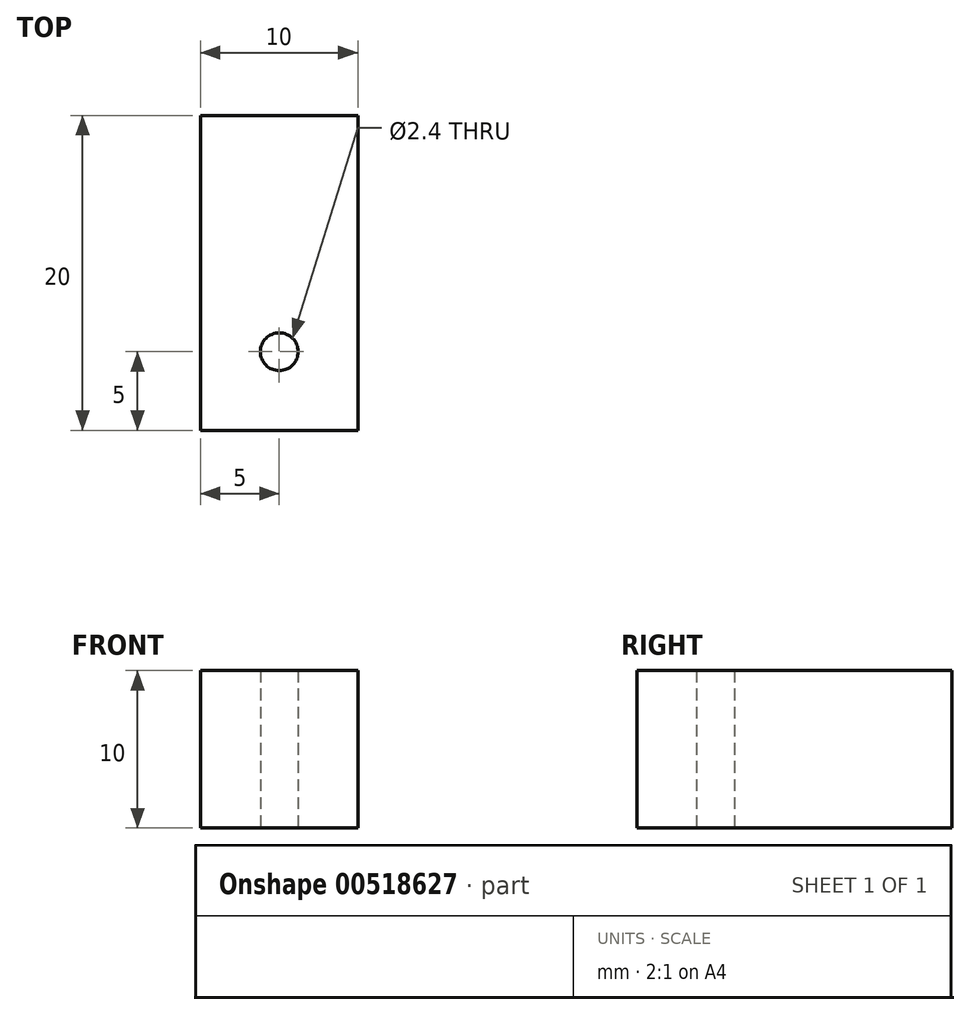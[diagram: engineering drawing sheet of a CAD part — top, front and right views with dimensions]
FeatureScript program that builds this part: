
annotation { "Feature Type Name" : "Feature", "Feature Type Description" : "" }
export const myFeature = defineFeature(function(context is Context, id is Id, definition is map)
    precondition{}
    {
        {
            var Q0;
            Q0=qCreatedBy(makeId("Top.planeOp"),FACE);
            var sketch = newSketch(context, id + "F0", { "sketchPlane" : qUnion([Q0])});
            skLineSegment(sketch, "E0.bottom", {"start": v(-5, 10) * mm, "end": v(5, 10) * mm});
            skLineSegment(sketch, "E0.top", {"start": v(-5, -10) * mm, "end": v(5, -10) * mm});
            skLineSegment(sketch, "E0.left", {"start": v(-5, 10) * mm, "end": v(-5, -10) * mm});
            skLineSegment(sketch, "E0.right", {"start": v(5, 10) * mm, "end": v(5, -10) * mm});
            skPoint(sketch, "E0.middle", {"position": v(0, 0) * mm});
            skCircle(sketch, "E1", {"center": v(0, -5) * mm, "radius": 1.2 * mm});
            skSolve(sketch);
        }
        {
            var Q0;
            Q0=makeQuery(id+"F0.imprint","IMPRINT",FACE,{"disambiguationData":[TD([[makeQuery(id+"F0.imprint","IMPRINT",EDGE,{"derivedFrom":sQuery(id+"F0.wireOp",EDGE,"E0.bottom")}),-1.0]])]});
            extrude(context, id + "F1", {"entities" : qUnion([Q0]), "depth" : 10 * mm, "offsetDistance" : 25 * mm});
        }
    });
